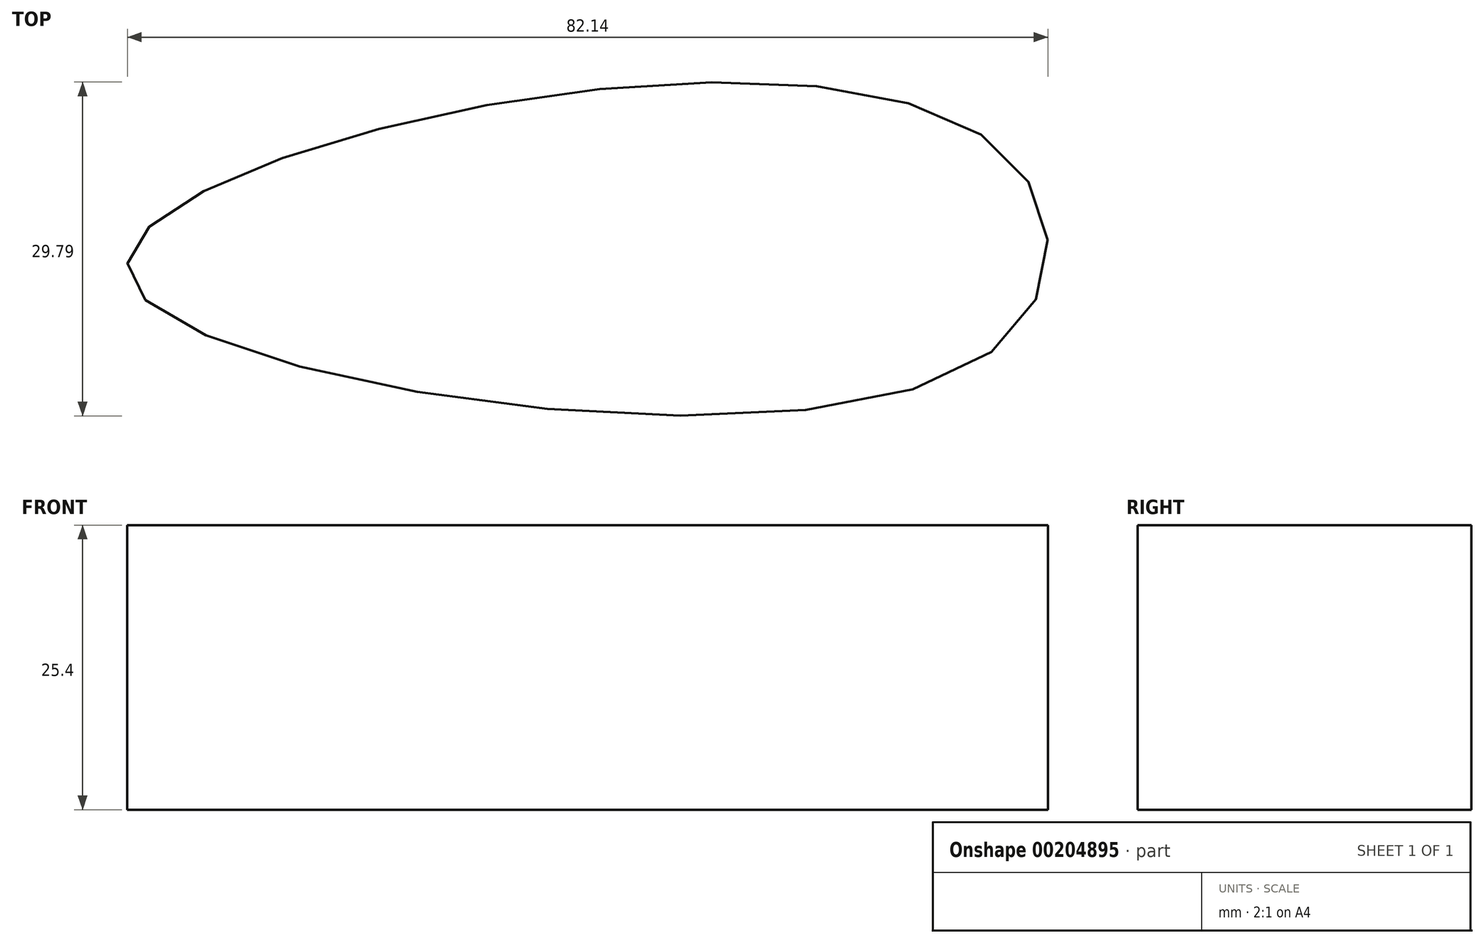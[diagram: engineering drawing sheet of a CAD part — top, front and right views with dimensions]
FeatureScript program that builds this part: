
annotation { "Feature Type Name" : "Feature", "Feature Type Description" : "" }
export const myFeature = defineFeature(function(context is Context, id is Id, definition is map)
    precondition{}
    {
        {
            var Q0;
            Q0=qCreatedBy(makeId("Top.planeOp"),FACE);
            var sketch = newSketch(context, id + "F0", { "sketchPlane" : qUnion([Q0])});
            skFitSpline(sketch, "E0", {"points": [v(0, 9.12) * mm, v(-12.8, -3) * mm, v(61.36, -9.44) * mm, v(63.73, 10.18) * mm, v(0, 9.12) * mm]});
            skSolve(sketch);
        }
        {
            var Q0;
            Q0 = qSketchRegion(id + "F0", true);
            extrude(context, id + "F1", {"entities" : qUnion([Q0]), "depth" : 12.7 * mm});
        }
        {
            var Q0;
            Q0 = qSketchRegion(id + "F0", true);
            extrude(context, id + "F2", {"entities" : qUnion([Q0]), "operationType" : NewBodyOperationType.ADD, "depth" : 25.4 * mm});
        }
    });
